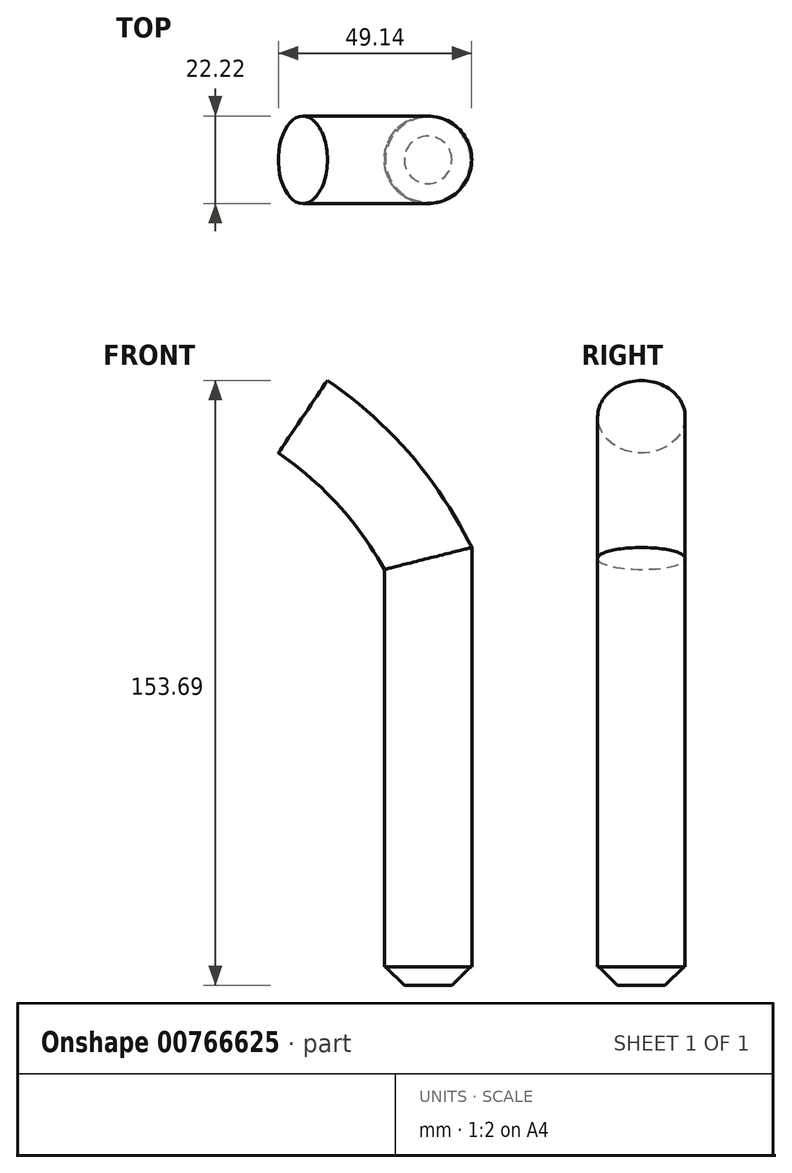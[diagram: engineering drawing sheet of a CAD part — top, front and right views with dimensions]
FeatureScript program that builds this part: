
annotation { "Feature Type Name" : "Feature", "Feature Type Description" : "" }
export const myFeature = defineFeature(function(context is Context, id is Id, definition is map)
    precondition{}
    {
        {
            var Q0;
            Q0=qCreatedBy(makeId("Front.planeOp"),FACE);
            var sketch = newSketch(context, id + "F0", { "sketchPlane" : qUnion([Q0])});
            skLineSegment(sketch, "E0", {"start": v(75.05, -88.32) * mm, "end": v(75.05, 18.36) * mm});
            skArc(sketch, "E1", {"start": v(75.05, 18.36) * mm, "mid": v(62.69, 35.98) * mm, "end": v(46.45, 50.13) * mm});
            skSolve(sketch);
        }
        {
            var Q0;
            Q0=qCreatedBy(makeId("Top.planeOp"),FACE);
            var sketch = newSketch(context, id + "F1", { "sketchPlane" : qUnion([Q0])});
            skCircle(sketch, "E2", {"center": v(82.35, 0) * mm, "radius": 11.11 * mm});
            skSolve(sketch);
        }
        {
            var Q0;
            Q0=makeQuery(id+"F1.imprint","IMPRINT",FACE,{"disambiguationData":[TD([[makeQuery(id+"F1.imprint","IMPRINT",EDGE,{"derivedFrom":sQuery(id+"F1.wireOp",EDGE,"E2")}),1.0]])]});
            var Q1;
            Q1=sQuery(id+"F0.wireOp",EDGE,"E1");
            var Q2;
            Q2=sQuery(id+"F0.wireOp",EDGE,"E0");
            sweep(context, id + "F2", {"profiles" : qUnion([Q0]), "path" : qUnion([Q1, Q2])});
        }
        {
            var Q0;
            Q0=makeQuery(id+"F2.opSweep","CAP_FACE",FACE,{"disambiguationData":[OSD([sQuery(id+"F0.wireOp",VERTEX,"E0.start"),sQuery(id+"F1.wireOp",EDGE,"E2")])],"isStart":true});
            chamfer(context, id + "F3", {"entities" : qUnion([Q0]), "width" : 5.08 * mm, "tangentPropagation" : true});
        }
        {
            var Q0;
            Q0 = qSketchRegion(id + "F1", true);
            extrude(context, id + "F4", {"entities" : qUnion([Q0]), "operationType" : NewBodyOperationType.ADD, "oppositeDirection" : true, "depth" : 83.57 * mm, "offsetDistance" : 25.4 * mm});
        }
    });
